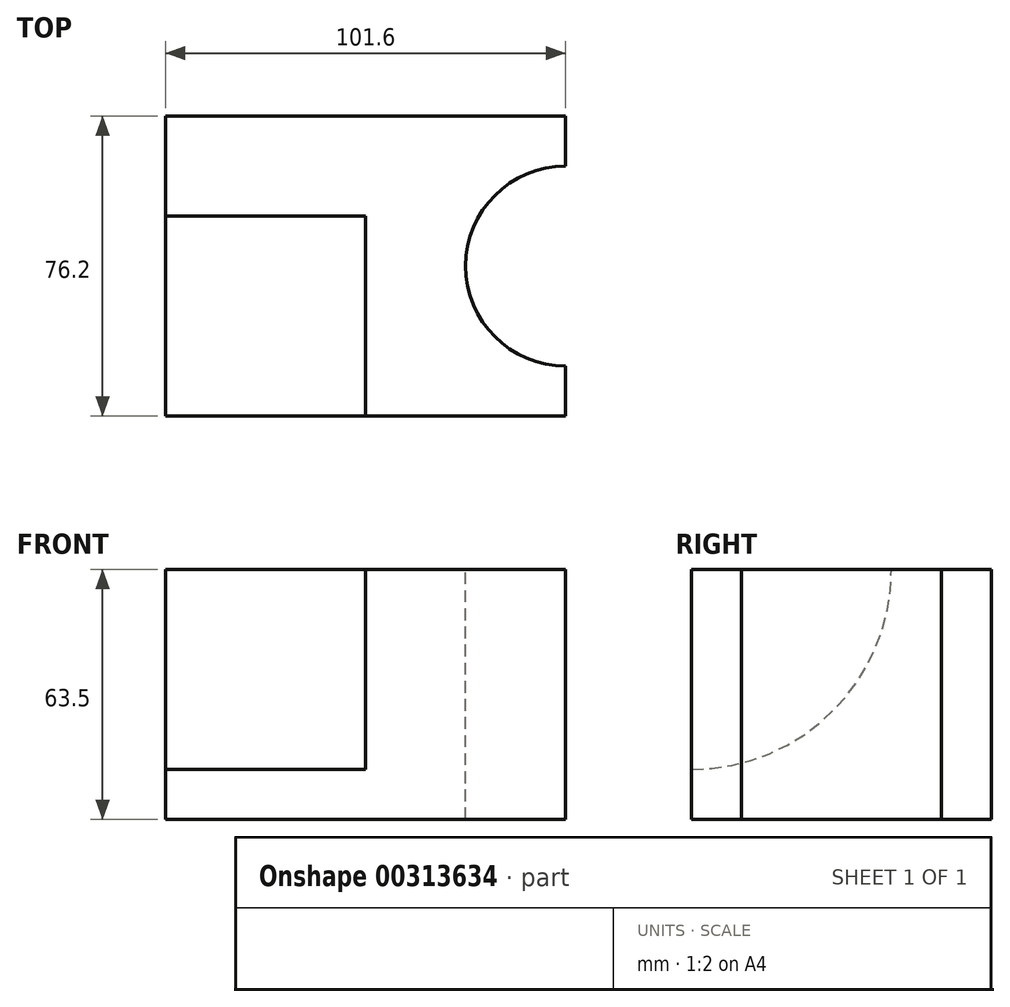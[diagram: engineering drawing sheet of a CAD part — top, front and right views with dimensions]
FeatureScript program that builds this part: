
annotation { "Feature Type Name" : "Feature", "Feature Type Description" : "" }
export const myFeature = defineFeature(function(context is Context, id is Id, definition is map)
    precondition{}
    {
        {
            var Q0;
            Q0=qCreatedBy(makeId("Top.planeOp"),FACE);
            var sketch = newSketch(context, id + "F0", { "sketchPlane" : qUnion([Q0])});
            skLineSegment(sketch, "E0", {"start": v(-44.75, 43.65) * mm, "end": v(56.85, 43.65) * mm});
            skLineSegment(sketch, "E1", {"start": v(56.85, 43.65) * mm, "end": v(56.85, -32.55) * mm});
            skLineSegment(sketch, "E2", {"start": v(56.85, -32.55) * mm, "end": v(-44.75, -32.55) * mm});
            skLineSegment(sketch, "E3", {"start": v(-44.75, -32.55) * mm, "end": v(-44.75, 43.65) * mm});
            skSolve(sketch);
        }
        {
            var Q0;
            Q0 = qSketchRegion(id + "F0", true);
            extrude(context, id + "F1", {"entities" : qUnion([Q0]), "depth" : 63.5 * mm});
        }
        {
            var Q0;
            Q0=makeQuery(id+"F1.opExtrude","CAP_FACE",FACE,{"disambiguationData":[OSD([sQuery(id+"F0.wireOp",EDGE,"E0"),sQuery(id+"F0.wireOp",EDGE,"E1"),sQuery(id+"F0.wireOp",EDGE,"E2"),sQuery(id+"F0.wireOp",EDGE,"E3")])],"isStart":false});
            var sketch = newSketch(context, id + "F2", { "sketchPlane" : qUnion([Q0])});
            skArc(sketch, "E4", {"start": v(56.85, 30.95) * mm, "mid": v(31.45, 5.55) * mm, "end": v(56.85, -19.85) * mm});
            skSolve(sketch);
        }
        {
            var Q0;
            {var subQ0=sQuery(id+"F2.wireOp",EDGE,"E4");Q0=makeQuery(id+"F2.imprint","IMPRINT",FACE,{"disambiguationData":[TD([[makeQuery(id+"F2.imprint","IMPRINT",EDGE,{"derivedFrom":subQ0}),1.0]])]});}
            extrude(context, id + "F3", {"entities" : qUnion([Q0]), "operationType" : NewBodyOperationType.REMOVE, "endBound" : BoundingType.THROUGH_ALL, "oppositeDirection" : true, "depth" : 25.4 * mm});
        }
        {
            var Q0;
            Q0=makeQuery(id+"F1.opExtrude","SWEPT_FACE",FACE,{"disambiguationData":[OSD([sQuery(id+"F0.wireOp",EDGE,"E3")])]});
            var sketch = newSketch(context, id + "F4", { "sketchPlane" : qUnion([Q0])});
            skArc(sketch, "E5", {"start": v(-18.25, 63.5) * mm, "mid": v(-3.37, 27.58) * mm, "end": v(32.55, 12.7) * mm});
            skSolve(sketch);
        }
        {
            var Q0;
            {var subQ0=sQuery(id+"F4.wireOp",EDGE,"E5");Q0=makeQuery(id+"F4.imprint","IMPRINT",FACE,{"disambiguationData":[TD([[makeQuery(id+"F4.imprint","IMPRINT",EDGE,{"derivedFrom":subQ0}),1.0]])]});}
            extrude(context, id + "F5", {"entities" : qUnion([Q0]), "operationType" : NewBodyOperationType.REMOVE, "oppositeDirection" : true, "depth" : 50.8 * mm});
        }
    });
